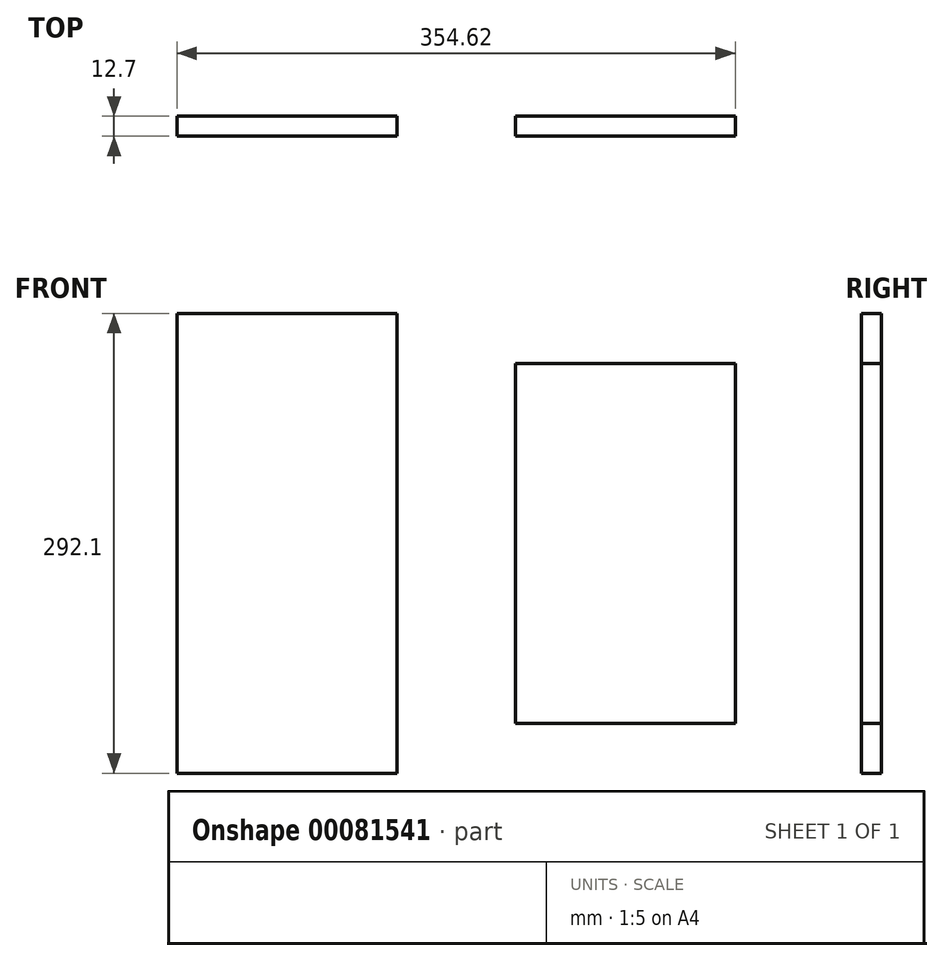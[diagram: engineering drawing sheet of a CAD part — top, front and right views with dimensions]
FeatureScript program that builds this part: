
annotation { "Feature Type Name" : "Feature", "Feature Type Description" : "" }
export const myFeature = defineFeature(function(context is Context, id is Id, definition is map)
    precondition{}
    {
        {
            var Q0;
            Q0=qCreatedBy(makeId("Front.planeOp"),FACE);
            var sketch = newSketch(context, id + "F0", { "sketchPlane" : qUnion([Q0])});
            skLineSegment(sketch, "E0.bottom", {"start": v(-171.94, 146.05) * mm, "end": v(-32.24, 146.05) * mm});
            skLineSegment(sketch, "E0.top", {"start": v(-171.94, -146.05) * mm, "end": v(-32.24, -146.05) * mm});
            skLineSegment(sketch, "E0.left", {"start": v(-171.94, 146.05) * mm, "end": v(-171.94, -146.05) * mm});
            skLineSegment(sketch, "E0.right", {"start": v(-32.24, 146.05) * mm, "end": v(-32.24, -146.05) * mm});
            skPoint(sketch, "E0.middle", {"position": v(-102.09, 0) * mm});
            skLineSegment(sketch, "E1.bottom", {"start": v(182.68, 114.3) * mm, "end": v(42.98, 114.3) * mm});
            skLineSegment(sketch, "E1.top", {"start": v(182.68, -114.3) * mm, "end": v(42.98, -114.3) * mm});
            skLineSegment(sketch, "E1.left", {"start": v(182.68, 114.3) * mm, "end": v(182.68, -114.3) * mm});
            skLineSegment(sketch, "E1.right", {"start": v(42.98, 114.3) * mm, "end": v(42.98, -114.3) * mm});
            skPoint(sketch, "E1.middle", {"position": v(112.83, 0) * mm});
            skSolve(sketch);
        }
        {
            var Q0;
            Q0=makeQuery(id+"F0.imprint","IMPRINT",FACE,{"disambiguationData":[TD([[makeQuery(id+"F0.imprint","IMPRINT",EDGE,{"derivedFrom":sQuery(id+"F0.wireOp",EDGE,"E0.bottom")}),-1.0]])]});
            var Q1;
            Q1=makeQuery(id+"F0.imprint","IMPRINT",FACE,{"disambiguationData":[TD([[makeQuery(id+"F0.imprint","IMPRINT",EDGE,{"derivedFrom":sQuery(id+"F0.wireOp",EDGE,"E1.bottom")}),1.0]])]});
            extrude(context, id + "F1", {"entities" : qUnion([Q0, Q1]), "depth" : 12.7 * mm});
        }
    });
